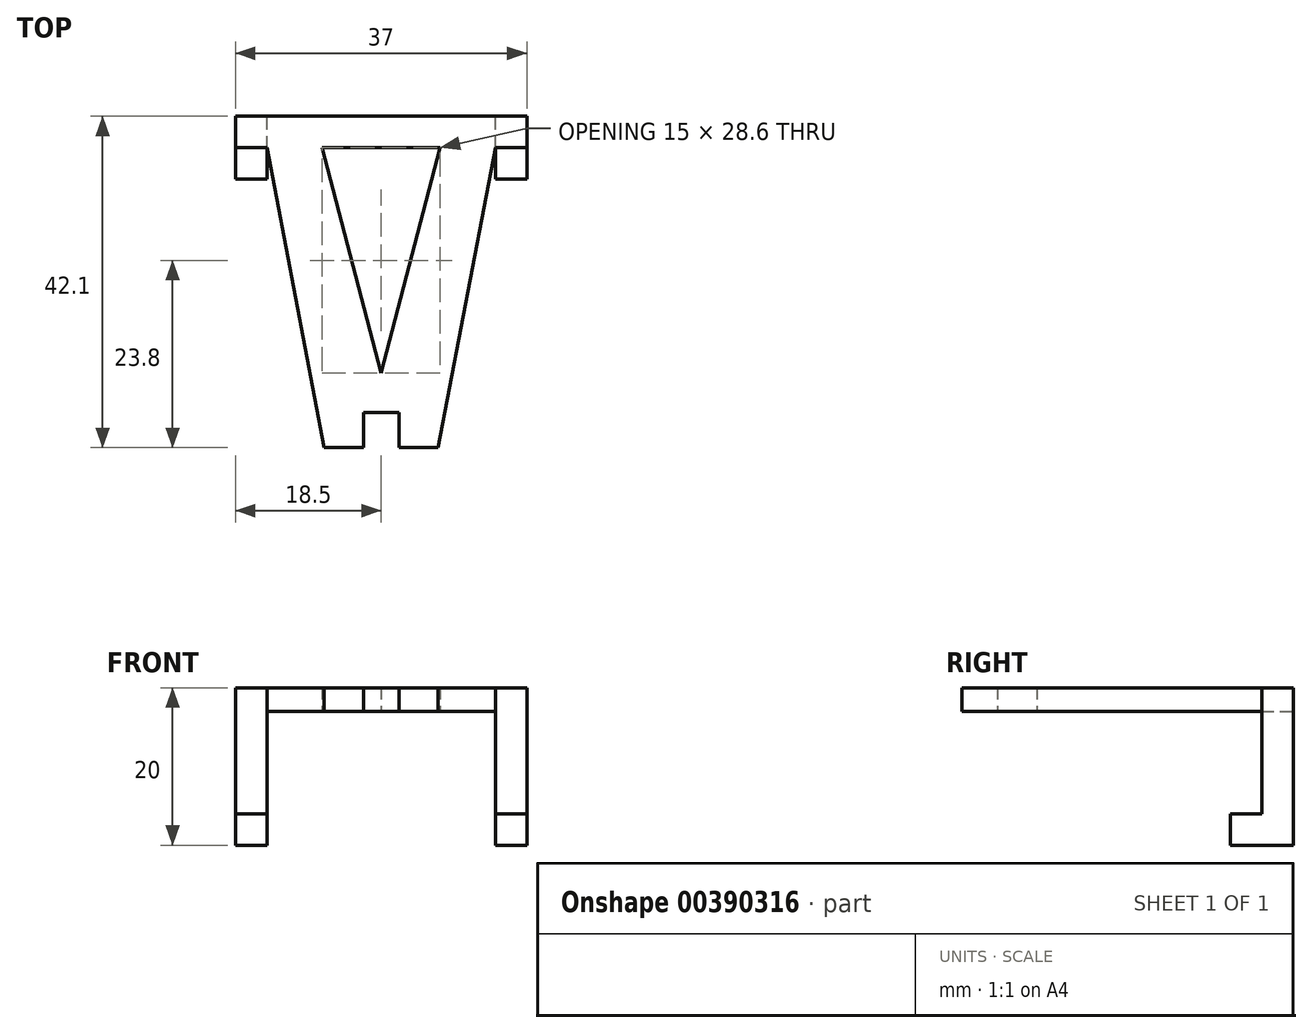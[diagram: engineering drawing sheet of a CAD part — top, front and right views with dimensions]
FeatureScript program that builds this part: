
annotation { "Feature Type Name" : "Feature", "Feature Type Description" : "" }
export const myFeature = defineFeature(function(context is Context, id is Id, definition is map)
    precondition{}
    {
        {
            var Q0;
            Q0=qCreatedBy(makeId("Top.planeOp"),FACE);
            var sketch = newSketch(context, id + "F0", { "sketchPlane" : qUnion([Q0])});
            skLineSegment(sketch, "E0.bottom", {"start": v(-14.5, 17.05) * mm, "end": v(14.5, 17.05) * mm});
            skLineSegment(sketch, "E0.top", {"start": v(-14.5, -21.05) * mm, "end": v(14.5, -21.05) * mm});
            skLineSegment(sketch, "E0.left", {"start": v(-14.5, 17.05) * mm, "end": v(-14.5, -21.05) * mm});
            skLineSegment(sketch, "E0.right", {"start": v(14.5, 17.05) * mm, "end": v(14.5, -21.05) * mm});
            skLineSegment(sketch, "E1.bottom", {"start": v(-18.5, 21.05) * mm, "end": v(18.5, 21.05) * mm});
            skLineSegment(sketch, "E1.top", {"start": v(-18.5, 17.05) * mm, "end": v(18.5, 17.05) * mm});
            skLineSegment(sketch, "E1.left", {"start": v(-18.5, 21.05) * mm, "end": v(-18.5, 17.05) * mm});
            skLineSegment(sketch, "E1.right", {"start": v(18.5, 21.05) * mm, "end": v(18.5, 17.05) * mm});
            skLineSegment(sketch, "E2.bottom", {"start": v(2.25, -21.05) * mm, "end": v(-2.25, -21.05) * mm});
            skLineSegment(sketch, "E2.top", {"start": v(2.25, -16.55) * mm, "end": v(-2.25, -16.55) * mm});
            skLineSegment(sketch, "E2.left", {"start": v(2.25, -21.05) * mm, "end": v(2.25, -16.55) * mm});
            skLineSegment(sketch, "E2.right", {"start": v(-2.25, -21.05) * mm, "end": v(-2.25, -16.55) * mm});
            skLineSegment(sketch, "E3", {"start": v(-14.5, 17.05) * mm, "end": v(-7.25, -21.05) * mm});
            skLineSegment(sketch, "E4", {"start": v(-7.25, -21.05) * mm, "end": v(-14.5, -21.05) * mm});
            skLineSegment(sketch, "E5", {"start": v(14.5, 17.05) * mm, "end": v(7.25, -21.05) * mm});
            skLineSegment(sketch, "E6", {"start": v(7.25, -21.05) * mm, "end": v(14.5, -21.05) * mm});
            skSolve(sketch);
        }
        {
            var Q0;
            {var subQ5=sQuery(id+"F0.wireOp",EDGE,"E1.left");Q0=makeQuery(id+"F0.imprint","IMPRINT",FACE,{"disambiguationData":[TD([[makeQuery(id+"F0.imprint","IMPRINT",EDGE,{"derivedFrom":subQ5}),1.0]])]});}
            var Q1;
            {var subQ5=sQuery(id+"F0.wireOp",EDGE,"E1.right");Q1=makeQuery(id+"F0.imprint","IMPRINT",FACE,{"disambiguationData":[TD([[makeQuery(id+"F0.imprint","IMPRINT",EDGE,{"derivedFrom":subQ5}),-1.0]])]});}
            var Q2;
            {var subQ0=sQuery(id+"F0.wireOp",EDGE,"E1.bottom");var subQ1=sQuery(id+"F0.wireOp",EDGE,"E0.left");var subQ2=makeQuery(id+"F0.imprint","INTERSECT",VERTEX,{"derivedFrom":[subQ1,subQ0]});Q2=makeQuery(id+"F0.imprint","IMPRINT",FACE,{"disambiguationData":[TD([[makeQuery(id+"F0.imprint","IMPRINT",EDGE,{"disambiguationData":[TD([[subQ2,-1.0]])],"derivedFrom":subQ0}),-1.0]])]});}
            var Q3;
            Q3=makeQuery(id+"F0.imprint","IMPRINT",FACE,{"disambiguationData":[TD([[makeQuery(id+"F0.imprint","IMPRINT",EDGE,{"derivedFrom":sQuery(id+"F0.wireOp",EDGE,"E2.top")}),-1.0]])]});
            var Q4;
            {var subQ0=sQuery(id+"F0.wireOp",EDGE,"E0.bottom");Q4=makeQuery(id+"F0.imprint","IMPRINT",FACE,{"disambiguationData":[TD([[makeQuery(id+"F0.imprint","IMPRINT",EDGE,{"derivedFrom":subQ0}),-1.0]])]});}
            extrude(context, id + "F1", {"entities" : qUnion([Q0, Q1, Q2, Q3, Q4]), "depth" : 3 * mm});
        }
        {
            var Q0;
            Q0=qCreatedBy(makeId("Right.planeOp"),FACE);
            var sketch = newSketch(context, id + "F2", { "sketchPlane" : qUnion([Q0])});
            skLineSegment(sketch, "E7", {"start": v(21.05, 0) * mm, "end": v(21.05, -13) * mm});
            skLineSegment(sketch, "E8", {"start": v(21.05, -13) * mm, "end": v(17.05, -13) * mm});
            skLineSegment(sketch, "E9", {"start": v(17.05, -13) * mm, "end": v(17.05, 0) * mm});
            skLineSegment(sketch, "E10", {"start": v(17.05, 0) * mm, "end": v(21.05, 0) * mm});
            skLineSegment(sketch, "E11", {"start": v(17.05, -13) * mm, "end": v(13.05, -13) * mm});
            skLineSegment(sketch, "E12", {"start": v(13.05, -13) * mm, "end": v(13.05, -17) * mm});
            skLineSegment(sketch, "E13", {"start": v(13.05, -17) * mm, "end": v(21.05, -17) * mm});
            skLineSegment(sketch, "E14", {"start": v(21.05, -17) * mm, "end": v(21.05, -13) * mm});
            skSolve(sketch);
        }
        {
            var Q0;
            Q0 = qSketchRegion(id + "F2", true);
            extrude(context, id + "F3", {"entities" : qUnion([Q0]), "operationType" : NewBodyOperationType.ADD, "depth" : (37 / 2) * mm, "hasSecondDirection" : true, "secondDirectionOppositeDirection" : false, "secondDirectionDepth" : 14.5 * mm});
        }
        {
            var Q0;
            Q0=makeQuery(id+"F1.opExtrude","SWEPT_BODY",BODY,{"disambiguationData":[OSD([sQuery(id+"F0.wireOp",EDGE,"E0.top"),sQuery(id+"F0.wireOp",EDGE,"E1.bottom"),sQuery(id+"F0.wireOp",EDGE,"E1.top"),sQuery(id+"F0.wireOp",EDGE,"E1.left"),sQuery(id+"F0.wireOp",EDGE,"E1.right"),sQuery(id+"F0.wireOp",EDGE,"E2.top"),sQuery(id+"F0.wireOp",EDGE,"E2.left"),sQuery(id+"F0.wireOp",EDGE,"E2.right"),sQuery(id+"F0.wireOp",EDGE,"E3"),sQuery(id+"F0.wireOp",EDGE,"E5"),sQuery(id+"F0.wireOp",EDGE,"Jtv9T4cj-stgb-gjOm-VE7l-2tUlwno8qtbM"),sQuery(id+"F0.wireOp",EDGE,"Qov7meJo-6eWo-KcaG-ylEU-tiCFja3HgiUB"),sQuery(id+"F0.wireOp",EDGE,"OMjmx1dL-pNHH-0urV-2AOd-FvDafvh0dZXW"),sQuery(id+"F0.wireOp",EDGE,"rHDhIWn5-BIgW-OLOp-uymO-odCV4Zoi0zfK")])]});
            var Q1;
            Q1=qCreatedBy(makeId("Right.planeOp"),FACE);
            mirror(context, id + "F4", {"operationType" : NewBodyOperationType.ADD, "entities" : qUnion([Q0]), "mirrorPlane" : qUnion([Q1])});
        }
        {
            var Q0;
            Q0=qCreatedBy(makeId("Top.planeOp"),FACE);
            var sketch = newSketch(context, id + "F5", { "sketchPlane" : qUnion([Q0])});
            skLineSegment(sketch, "E15", {"start": v(-7.5, 17.05) * mm, "end": v(0, -11.55) * mm});
            skLineSegment(sketch, "E16", {"start": v(0, -11.55) * mm, "end": v(7.5, 17.05) * mm});
            skLineSegment(sketch, "E17", {"start": v(7.5, 17.05) * mm, "end": v(-7.5, 17.05) * mm});
            skSolve(sketch);
        }
        {
            var Q0;
            Q0 = qSketchRegion(id + "F5", true);
            extrude(context, id + "F6", {"entities" : qUnion([Q0]), "operationType" : NewBodyOperationType.REMOVE, "depth" : 25 * mm});
        }
    });
